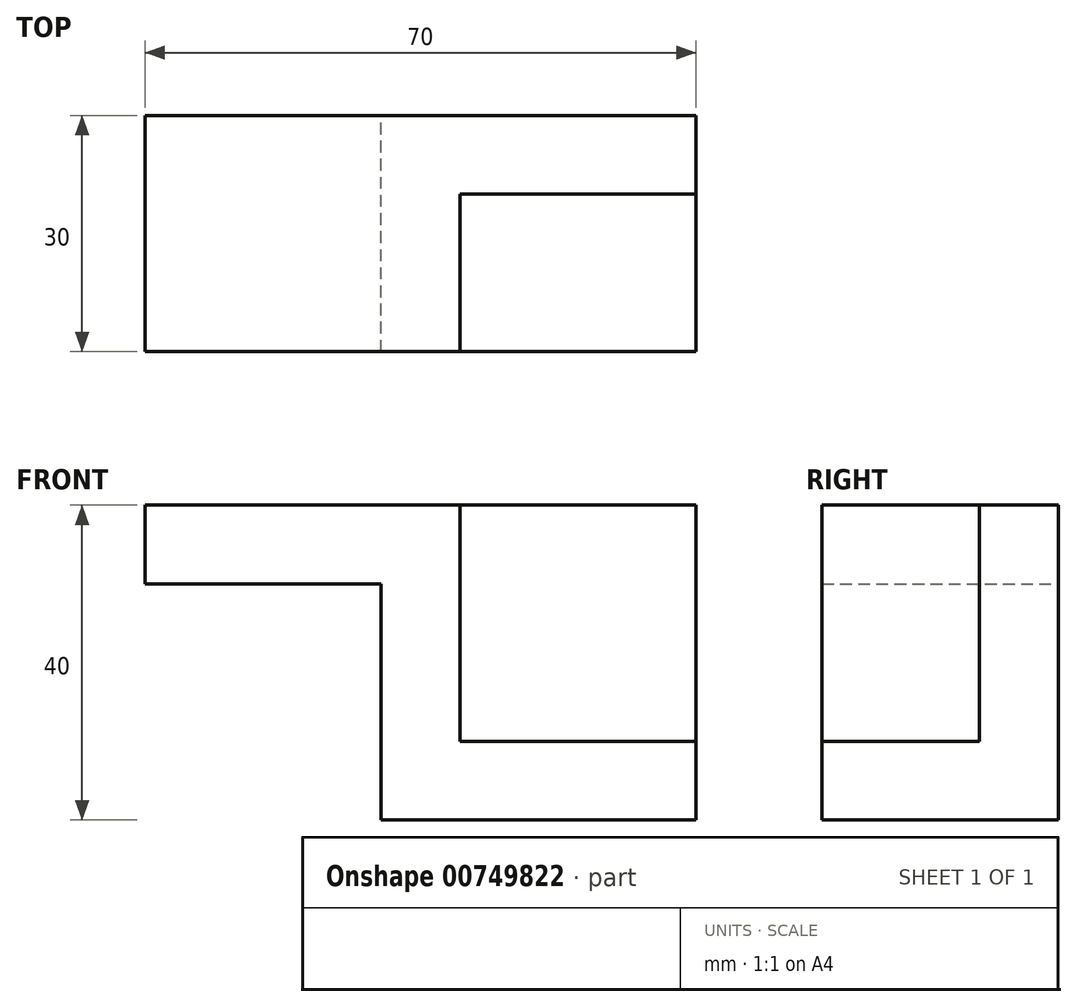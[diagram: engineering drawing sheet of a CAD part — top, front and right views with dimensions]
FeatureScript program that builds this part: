
annotation { "Feature Type Name" : "Feature", "Feature Type Description" : "" }
export const myFeature = defineFeature(function(context is Context, id is Id, definition is map)
    precondition{}
    {
        {
            var Q0;
            Q0=qCreatedBy(makeId("Top.planeOp"),FACE);
            var sketch = newSketch(context, id + "F0", { "sketchPlane" : qUnion([Q0])});
            skLineSegment(sketch, "E0.bottom", {"start": v(0, 0) * mm, "end": v(40, 0) * mm});
            skLineSegment(sketch, "E0.top", {"start": v(0, 30) * mm, "end": v(40, 30) * mm});
            skLineSegment(sketch, "E0.left", {"start": v(0, 0) * mm, "end": v(0, 30) * mm});
            skLineSegment(sketch, "E0.right", {"start": v(40, 0) * mm, "end": v(40, 30) * mm});
            skSolve(sketch);
        }
        {
            var Q0;
            Q0=makeQuery(id+"F0.imprint","IMPRINT",FACE,{"disambiguationData":[TD([[makeQuery(id+"F0.imprint","IMPRINT",EDGE,{"derivedFrom":sQuery(id+"F0.wireOp",EDGE,"E0.bottom")}),1.0]])]});
            extrude(context, id + "F1", {"entities" : qUnion([Q0]), "depth" : 40 * mm, "offsetDistance" : 25 * mm});
        }
        {
            var Q0;
            Q0=makeQuery(id+"F1.opExtrude","CAP_FACE",FACE,{"disambiguationData":[OSD([sQuery(id+"F0.wireOp",EDGE,"E0.bottom"),sQuery(id+"F0.wireOp",EDGE,"E0.top"),sQuery(id+"F0.wireOp",EDGE,"E0.left"),sQuery(id+"F0.wireOp",EDGE,"E0.right")])],"isStart":false});
            var sketch = newSketch(context, id + "F2", { "sketchPlane" : qUnion([Q0])});
            skLineSegment(sketch, "E1", {"start": v(0, 0) * mm, "end": v(10, 0) * mm});
            skLineSegment(sketch, "E2", {"start": v(10, 0) * mm, "end": v(10, 20) * mm});
            skLineSegment(sketch, "E3", {"start": v(10, 20) * mm, "end": v(40, 20) * mm});
            skLineSegment(sketch, "E4", {"start": v(40, 20) * mm, "end": v(40, 30) * mm});
            skLineSegment(sketch, "E5", {"start": v(40, 30) * mm, "end": v(0, 30) * mm});
            skLineSegment(sketch, "E6", {"start": v(0, 30) * mm, "end": v(0, 0) * mm});
            skLineSegment(sketch, "E7", {"start": v(40, 20) * mm, "end": v(40, 0) * mm});
            skLineSegment(sketch, "E8", {"start": v(40, 0) * mm, "end": v(10, 0) * mm});
            skSolve(sketch);
        }
        {
            var Q0;
            Q0=makeQuery(id+"F2.imprint","IMPRINT",FACE,{"disambiguationData":[TD([[makeQuery(id+"F2.imprint","IMPRINT",EDGE,{"derivedFrom":sQuery(id+"F2.wireOp",EDGE,"E2")}),-1.0]])]});
            extrude(context, id + "F3", {"entities" : qUnion([Q0]), "operationType" : NewBodyOperationType.REMOVE, "oppositeDirection" : true, "depth" : 30 * mm, "offsetDistance" : 25 * mm});
        }
        {
            var Q0;
            Q0=makeQuery(id+"F1.opExtrude","CAP_FACE",FACE,{"disambiguationData":[OSD([sQuery(id+"F0.wireOp",EDGE,"E0.bottom"),sQuery(id+"F0.wireOp",EDGE,"E0.top"),sQuery(id+"F0.wireOp",EDGE,"E0.left"),sQuery(id+"F0.wireOp",EDGE,"E0.right")])],"isStart":false});
            var sketch = newSketch(context, id + "F4", { "sketchPlane" : qUnion([Q0])});
            skLineSegment(sketch, "E9", {"start": v(0, 0) * mm, "end": v(-30, 0) * mm});
            skLineSegment(sketch, "E10", {"start": v(-30, 0) * mm, "end": v(-30, 30) * mm});
            skLineSegment(sketch, "E11", {"start": v(-30, 30) * mm, "end": v(0, 30) * mm});
            skLineSegment(sketch, "E12", {"start": v(0, 30) * mm, "end": v(0, 0) * mm});
            skSolve(sketch);
        }
        {
            var Q0;
            Q0=makeQuery(id+"F4.imprint","IMPRINT",FACE,{"disambiguationData":[TD([[makeQuery(id+"F4.imprint","IMPRINT",EDGE,{"derivedFrom":sQuery(id+"F4.wireOp",EDGE,"E9")}),-1.0]])]});
            extrude(context, id + "F5", {"entities" : qUnion([Q0]), "operationType" : NewBodyOperationType.ADD, "oppositeDirection" : true, "depth" : 10 * mm, "offsetDistance" : 25 * mm});
        }
    });
